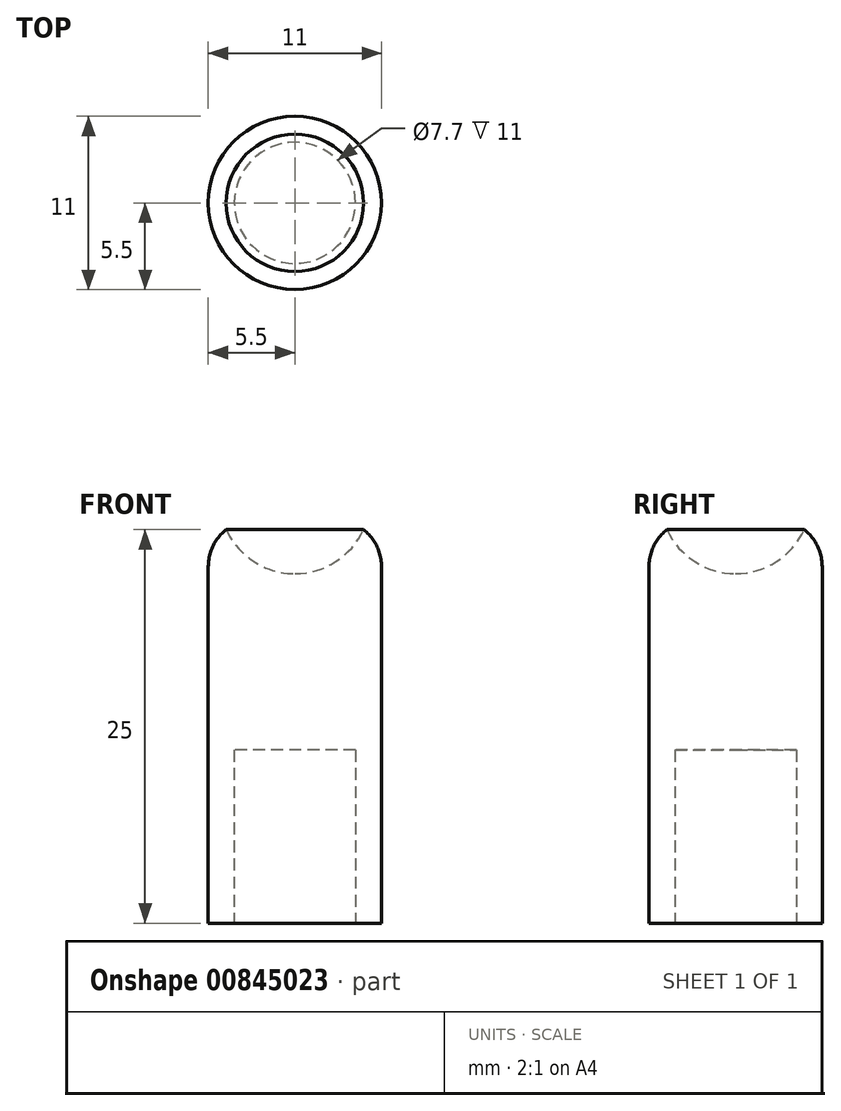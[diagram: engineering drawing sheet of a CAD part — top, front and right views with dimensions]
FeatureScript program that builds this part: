
annotation { "Feature Type Name" : "Feature", "Feature Type Description" : "" }
export const myFeature = defineFeature(function(context is Context, id is Id, definition is map)
    precondition{}
    {
        {
            var Q0;
            Q0=qCreatedBy(makeId("Top.planeOp"),FACE);
            var sketch = newSketch(context, id + "F0", { "sketchPlane" : qUnion([Q0])});
            skCircle(sketch, "E0", {"center": v(0, 0) * mm, "radius": 3.85 * mm});
            skCircle(sketch, "E1", {"center": v(0, 0) * mm, "radius": 5.5 * mm});
            skSolve(sketch);
        }
        {
            var Q0;
            Q0=makeQuery(id+"F0.imprint","IMPRINT",FACE,{"disambiguationData":[TD([[makeQuery(id+"F0.imprint","IMPRINT",EDGE,{"derivedFrom":sQuery(id+"F0.wireOp",EDGE,"E0")}),-1.0]])]});
            extrude(context, id + "F1", {"entities" : qUnion([Q0]), "depth" : 25 * mm, "offsetDistance" : 25 * mm});
        }
        {
            var Q0;
            Q0=makeQuery(id+"F0.imprint","IMPRINT",FACE,{"disambiguationData":[TD([[makeQuery(id+"F0.imprint","IMPRINT",EDGE,{"derivedFrom":sQuery(id+"F0.wireOp",EDGE,"E0")}),1.0]])]});
            extrude(context, id + "F2", {"entities" : qUnion([Q0]), "operationType" : NewBodyOperationType.ADD, "depth" : 25 * mm, "offsetDistance" : 25 * mm, "hasSecondDirection" : true, "secondDirectionOppositeDirection" : false, "secondDirectionDepth" : 11 * mm});
        }
        {
            var Q0;
            Q0=qCreatedBy(makeId("Front.planeOp"),FACE);
            var sketch = newSketch(context, id + "F3", { "sketchPlane" : qUnion([Q0])});
            skArc(sketch, "E2", {"start": v(0, 31.8) * mm, "mid": v(-4.8, 27) * mm, "end": v(0, 22.2) * mm});
            skLineSegment(sketch, "E3", {"start": v(0, 31.8) * mm, "end": v(0, 22.2) * mm});
            skSolve(sketch);
        }
        {
            var Q0;
            Q0=makeQuery(id+"F3.imprint","IMPRINT",FACE,{"disambiguationData":[TD([[makeQuery(id+"F3.imprint","IMPRINT",EDGE,{"derivedFrom":sQuery(id+"F3.wireOp",EDGE,"E2")}),1.0]])]});
            var Q1;
            Q1=sQuery(id+"F3.wireOp",EDGE,"E3");
            revolve(context, id + "F4", {"operationType" : NewBodyOperationType.REMOVE, "surfaceOperationType" : NewSurfaceOperationType.NEW, "entities" : qUnion([Q0]), "axis" : qUnion([Q1]), "revolveType" : RevolveType.FULL, "oppositeDirection" : true});
        }
        {
            var Q0;
            Q0=makeQuery(id+"F1.opExtrude","CAP_EDGE",EDGE,{"disambiguationData":[OSD([sQuery(id+"F0.wireOp",EDGE,"E1")])],"isStart":false});
            fillet(context, id + "F5", {"entities" : qUnion([Q0]), "radius" : 3 * mm, "tangentPropagation" : true, "allowEdgeOverflow" : false});
        }
    });
